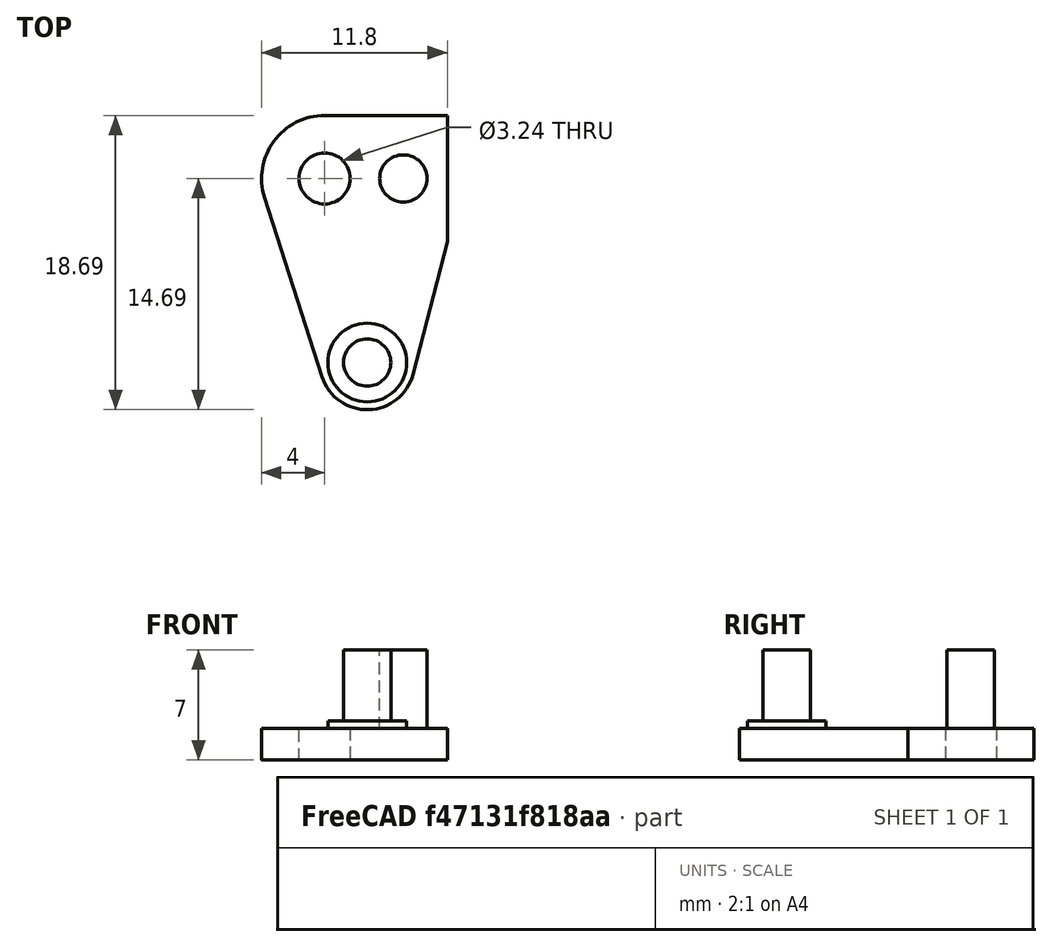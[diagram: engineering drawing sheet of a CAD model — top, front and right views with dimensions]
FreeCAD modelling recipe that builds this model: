
FCSTD DOCUMENT  (FreeCAD 1.0R39285 (Git))
Label: WheelLinkageBottomRight
License: All rights reserved
LicenseURL: https://en.wikipedia.org/wiki/All_rights_reserved
objects: PartDesign::SubShapeBinder×1, Part::Mirroring×1, App::Part×1
note: 2 computed .brp shape members not serialized (recipe doc carries the construction recipe); baked Part::Feature solids carry a one-line shape summary decoded from their .brp
EXTERNAL_REF file=WheelLinkageBottomLeft.FCStd obj=Part

FEATURE [PartDesign::SubShapeBinder] Binder  label="WheelLinkageBottomLeftBody"
  BindCopyOnChange = 0
  BindMode = 0
  ClaimChildren = false
  Context = -> Part [Binder.]
  Fuse = false
  MakeFace = true
  OffsetFill = false
  OffsetIntersection = false
  OffsetJoinType = 0
  OffsetOpenResult = false
  PartialLoad = false
  Refine = true
  Relative = true
  Support = -> [<external WheelLinkageBottomLeft.FCStd>#Part[Body.]]
  _Version = 2
FEATURE [Part::Mirroring] Part__Mirroring  label="WheelLinkageBottomRightBody"
  Base = (0,0,0)
  Normal = (1,0,0)
  Source = -> Binder
FEATURE [App::Part] Part  label="WheelLinkageBottomRightPart"
  Group = -> [Binder,Part__Mirroring]
  Origin = -> Origin
